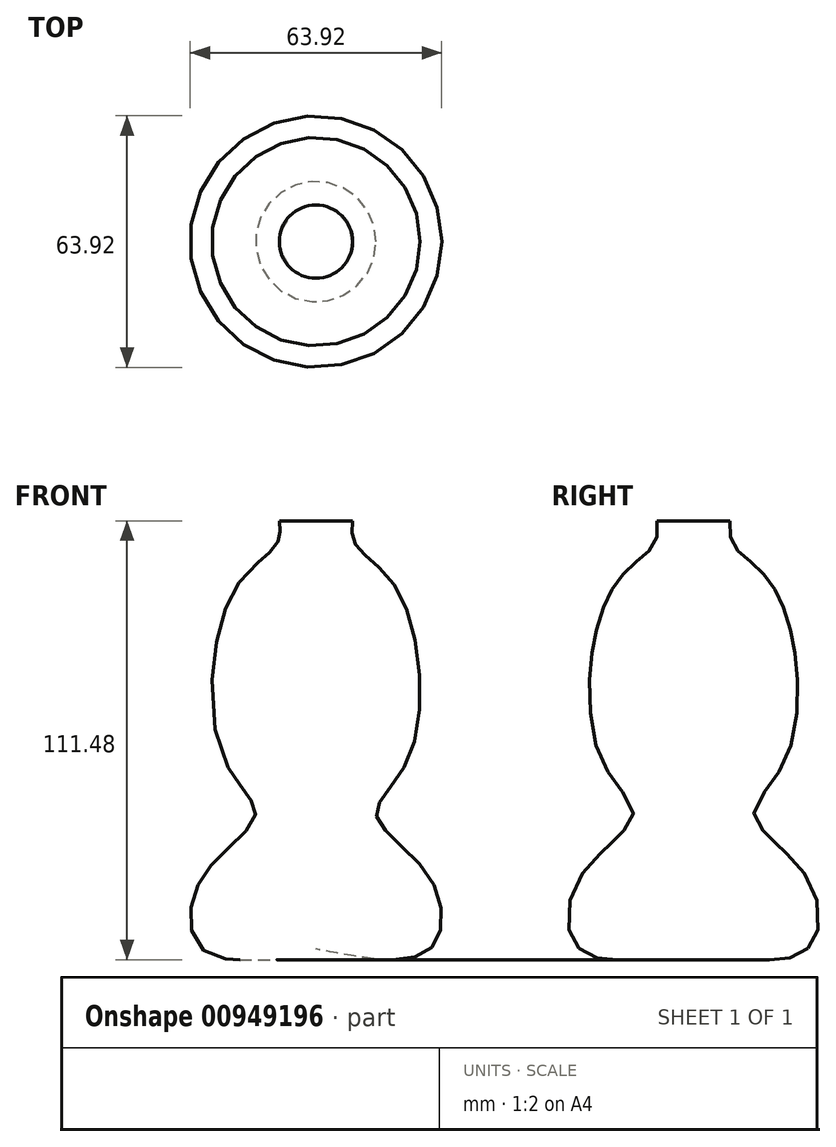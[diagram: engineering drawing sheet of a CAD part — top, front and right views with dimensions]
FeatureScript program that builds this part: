
annotation { "Feature Type Name" : "Feature", "Feature Type Description" : "" }
export const myFeature = defineFeature(function(context is Context, id is Id, definition is map)
    precondition{}
    {
        {
            var Q0;
            Q0=qCreatedBy(makeId("Front.planeOp"),FACE);
            var sketch = newSketch(context, id + "F0", { "sketchPlane" : qUnion([Q0])});
            skLineSegment(sketch, "E0", {"start": v(0, 60.82) * mm, "end": v(0, -40.86) * mm});
            skSolve(sketch);
        }
        {
            var Q0;
            Q0=qCreatedBy(makeId("Front.planeOp"),FACE);
            var sketch = newSketch(context, id + "F1", { "sketchPlane" : qUnion([Q0])});
            skFitSpline(sketch, "E1", {"points": [v(9.3, 60.05) * mm, v(10.06, 54) * mm, v(20.64, 42.67) * mm, v(23.66, 0) * mm, v(15.35, -14.73) * mm, v(28.95, -30.6) * mm, v(28.95, -48.72) * mm, v(0, -48.72) * mm], "startDerivative": vector(-7.06, -79.92) * mm, "endDerivative": vector(-207.33, 40.8) * mm});
            skSolve(sketch);
        }
        {
            var Q0;
            Q0 = qSketchRegion(id + "F1", true);
            var Q1;
            Q1=sQuery(id+"F1.wireOp",EDGE,"E1");
            var Q2;
            Q2=sQuery(id+"F0.wireOp",EDGE,"E0");
            revolve(context, id + "F2", {"bodyType" : ToolBodyType.SURFACE, "surfaceOperationType" : NewSurfaceOperationType.NEW, "entities" : qUnion([Q0]), "surfaceEntities" : qUnion([Q1]), "axis" : qUnion([Q2]), "revolveType" : RevolveType.FULL});
        }
    });
